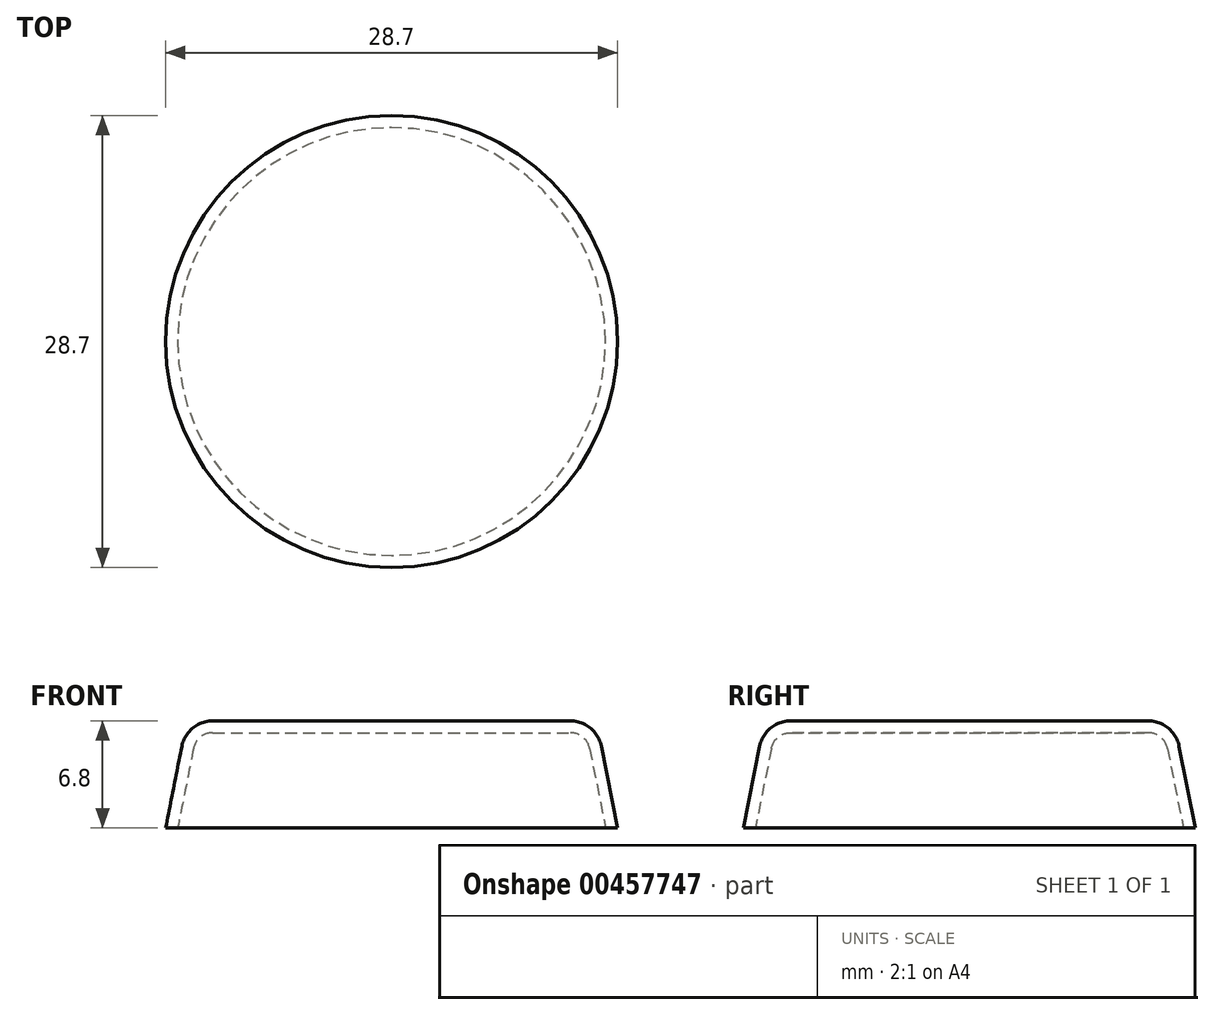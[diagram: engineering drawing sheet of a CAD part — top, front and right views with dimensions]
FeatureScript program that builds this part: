
annotation { "Feature Type Name" : "Feature", "Feature Type Description" : "" }
export const myFeature = defineFeature(function(context is Context, id is Id, definition is map)
    precondition{}
    {
        {
            var Q0;
            Q0=qCreatedBy(makeId("Front.planeOp"),FACE);
            var sketch = newSketch(context, id + "F0", { "sketchPlane" : qUnion([Q0])});
            skLineSegment(sketch, "E0", {"start": v(0, 0) * mm, "end": v(0, 6.8) * mm});
            skLineSegment(sketch, "E1", {"start": v(0, 6.8) * mm, "end": v(13, 6.8) * mm});
            skLineSegment(sketch, "E2", {"start": v(13, 6.8) * mm, "end": v(14.35, 0) * mm});
            skLineSegment(sketch, "E3", {"start": v(14.35, 0) * mm, "end": v(0, 0) * mm});
            skSolve(sketch);
        }
        {
            var Q0;
            Q0=makeQuery(id+"F0.imprint","IMPRINT",FACE,{"disambiguationData":[TD([[makeQuery(id+"F0.imprint","IMPRINT",EDGE,{"derivedFrom":sQuery(id+"F0.wireOp",EDGE,"E0")}),-1.0]])]});
            var Q1;
            Q1=sQuery(id+"F0.wireOp",EDGE,"E0");
            revolve(context, id + "F1", {"entities" : qUnion([Q0]), "axis" : qUnion([Q1]), "revolveType" : RevolveType.FULL});
        }
        {
            var Q0;
            Q0=makeQuery(id+"F1.opRevolve","SWEPT_EDGE",EDGE,{"disambiguationData":[OSD([sQuery(id+"F0.wireOp",EDGE,"E1"),sQuery(id+"F0.wireOp",EDGE,"E2")])]});
            fillet(context, id + "F2", {"entities" : qUnion([Q0]), "radius" : 2 * mm, "tangentPropagation" : true, "allowEdgeOverflow" : false});
        }
        {
            var Q0;
            Q0=makeQuery(id+"F1.opRevolve","SWEPT_FACE",FACE,{"disambiguationData":[OSD([sQuery(id+"F0.wireOp",EDGE,"E3")])]});
            shell(context, id + "F3", {"entities" : qUnion([Q0]), "thickness" : 0.75 * mm});
        }
    });
